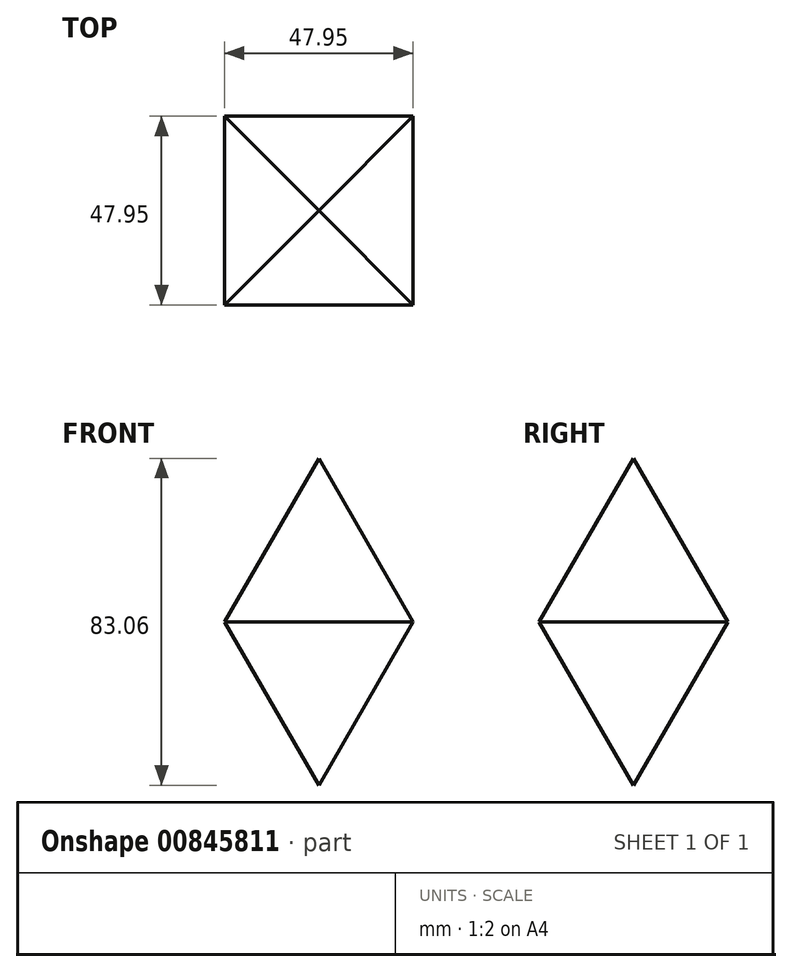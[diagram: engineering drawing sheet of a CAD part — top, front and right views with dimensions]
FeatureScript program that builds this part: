
annotation { "Feature Type Name" : "Feature", "Feature Type Description" : "" }
export const myFeature = defineFeature(function(context is Context, id is Id, definition is map)
    precondition{}
    {
        {
            var Q0;
            Q0=qCreatedBy(makeId("Top.planeOp"),FACE);
            var sketch = newSketch(context, id + "F0", { "sketchPlane" : qUnion([Q0])});
            skLineSegment(sketch, "E0.bottom", {"start": v(0, 0) * mm, "end": v(47.95, 0) * mm});
            skLineSegment(sketch, "E0.top", {"start": v(0, -47.95) * mm, "end": v(47.95, -47.95) * mm});
            skLineSegment(sketch, "E0.left", {"start": v(0, 0) * mm, "end": v(0, -47.95) * mm});
            skLineSegment(sketch, "E0.right", {"start": v(47.95, 0) * mm, "end": v(47.95, -47.95) * mm});
            skSolve(sketch);
        }
        {
            var Q0;
            Q0=makeQuery(id+"F0.imprint","IMPRINT",FACE,{"disambiguationData":[TD([[makeQuery(id+"F0.imprint","IMPRINT",EDGE,{"derivedFrom":sQuery(id+"F0.wireOp",EDGE,"E0.bottom")}),-1.0]])]});
            extrude(context, id + "F1", {"entities" : qUnion([Q0]), "oppositeDirection" : true, "depth" : 61.47 * mm, "offsetDistance" : 25.4 * mm, "hasDraft" : true, "draftAngle" : 30 * degree, "draftPullDirection" : true, "hasSecondDirection" : true, "secondDirectionOppositeDirection" : false, "secondDirectionDepth" : 57.15 * mm, "hasSecondDirectionDraft" : true, "secondDirectionDraftAngle" : 30 * degree, "secondDirectionDraftPullDirection" : true});
        }
    });
